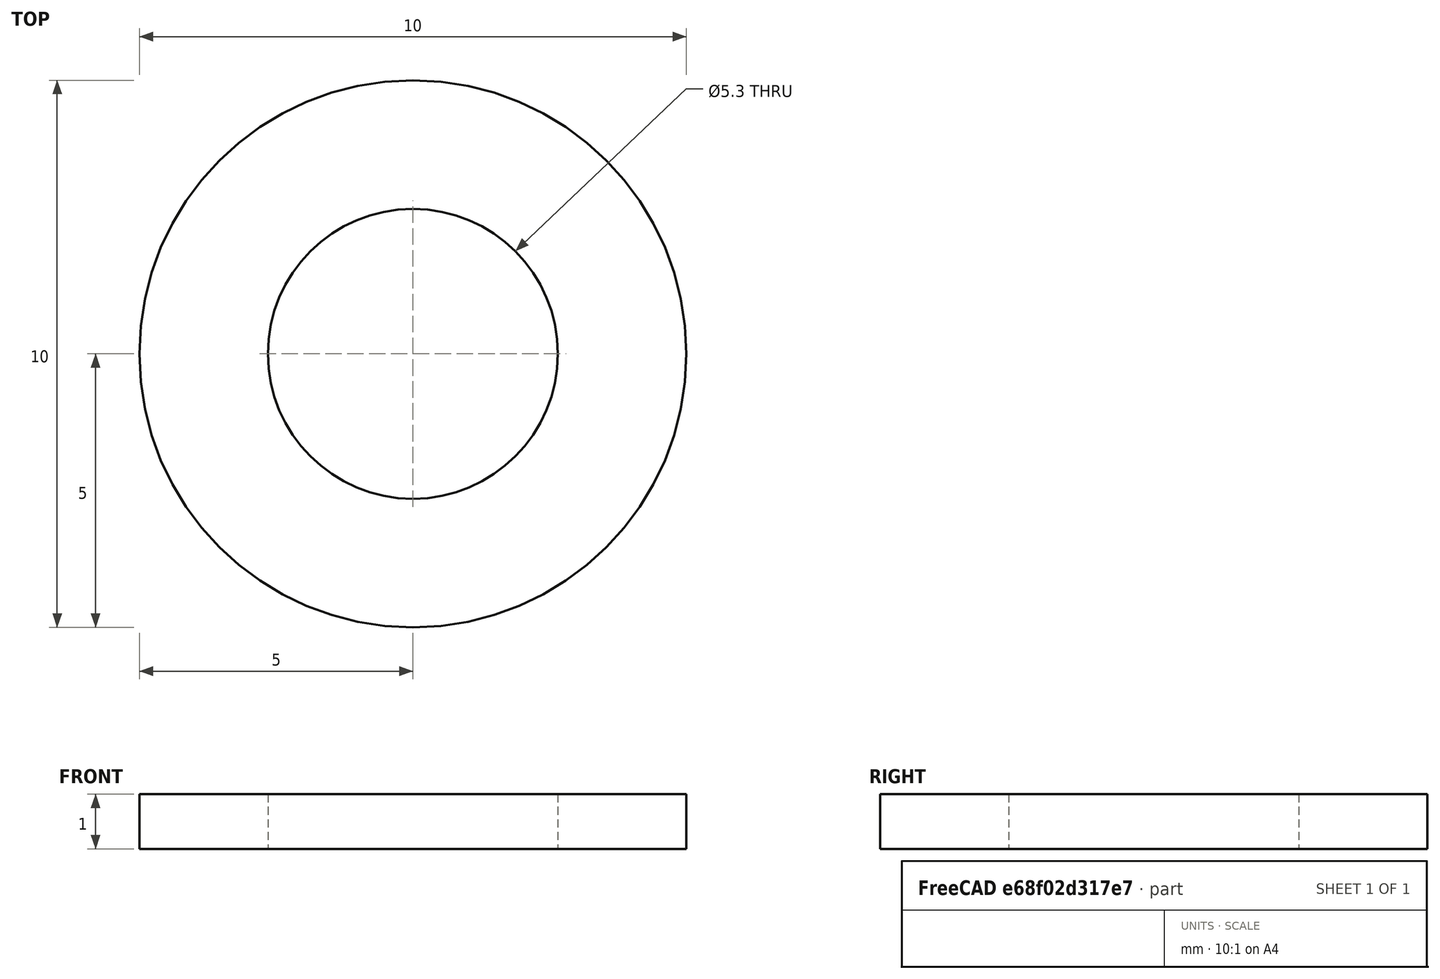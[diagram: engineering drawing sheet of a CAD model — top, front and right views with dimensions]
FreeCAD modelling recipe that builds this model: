
FCSTD DOCUMENT  (FreeCAD 0.14R3700 (Git))
Label: Scheibe DIN 125 - A 5,3
License: CC-BY 3.0
LicenseURL: http://creativecommons.org/licenses/by/3.0/
objects: Sketcher::SketchObject×1, PartDesign::Revolution×1, Part::Feature×1
note: 4 computed .brp shape members not serialized (recipe doc carries the construction recipe); baked Part::Feature solids carry a one-line shape summary decoded from their .brp

FEATURE [Sketcher::SketchObject] Sketch
  Placement = pos=(0,0,0) rot=(0.57735,0.57735,0.57735;2.0944rad)
  sketch-geometry (4):
    g0: LineSegment StartX=2.65 StartY=0 StartZ=0 EndX=5 EndY=0 EndZ=0
    g1: LineSegment StartX=5 StartY=0 StartZ=0 EndX=5 EndY=1 EndZ=0
    g2: LineSegment StartX=5 StartY=1 StartZ=0 EndX=2.65 EndY=1 EndZ=0
    g3: LineSegment StartX=2.65 StartY=1 StartZ=0 EndX=2.65 EndY=0 EndZ=0
  constraints (12):
    c: Coincident(g0,g1)
    c: Coincident(g1,g2)
    c: Coincident(g2,g3)
    c: Coincident(g3,g0)
    c: Horizontal(g0)
    c: Horizontal(g2)
    c: Vertical(g1)
    c: Vertical(g3)
    c: PointOnObject(g0,g-1)
    c: DistanceY(g1) = 1
    c: DistanceX(g-1,g2) = 2.65
    c: DistanceX(g-1,g1) = 5
FEATURE [PartDesign::Revolution] Revolution  label="Scheibe DIN 125 - A 5,3 #"
  Angle = 360
  Axis = (0,0,1)
  Base = (0,0,0)
  Placement = pos=(0,0,0) rot=(0.57735,0.57735,0.57735;2.0944rad)
  ReferenceAxis = -> Sketch [V_Axis]
  Reversed = true
  Sketch = -> Sketch
FEATURE [Part::Feature] Revolution001  label="Scheibe DIN 125 - A 5,3 #001"
  Placement = pos=(0,0,0) rot=(0.57735,0.57735,0.57735;2.0944rad)
  shape: bbox 10 x 10 x 1 mm, 4 faces (baked)
